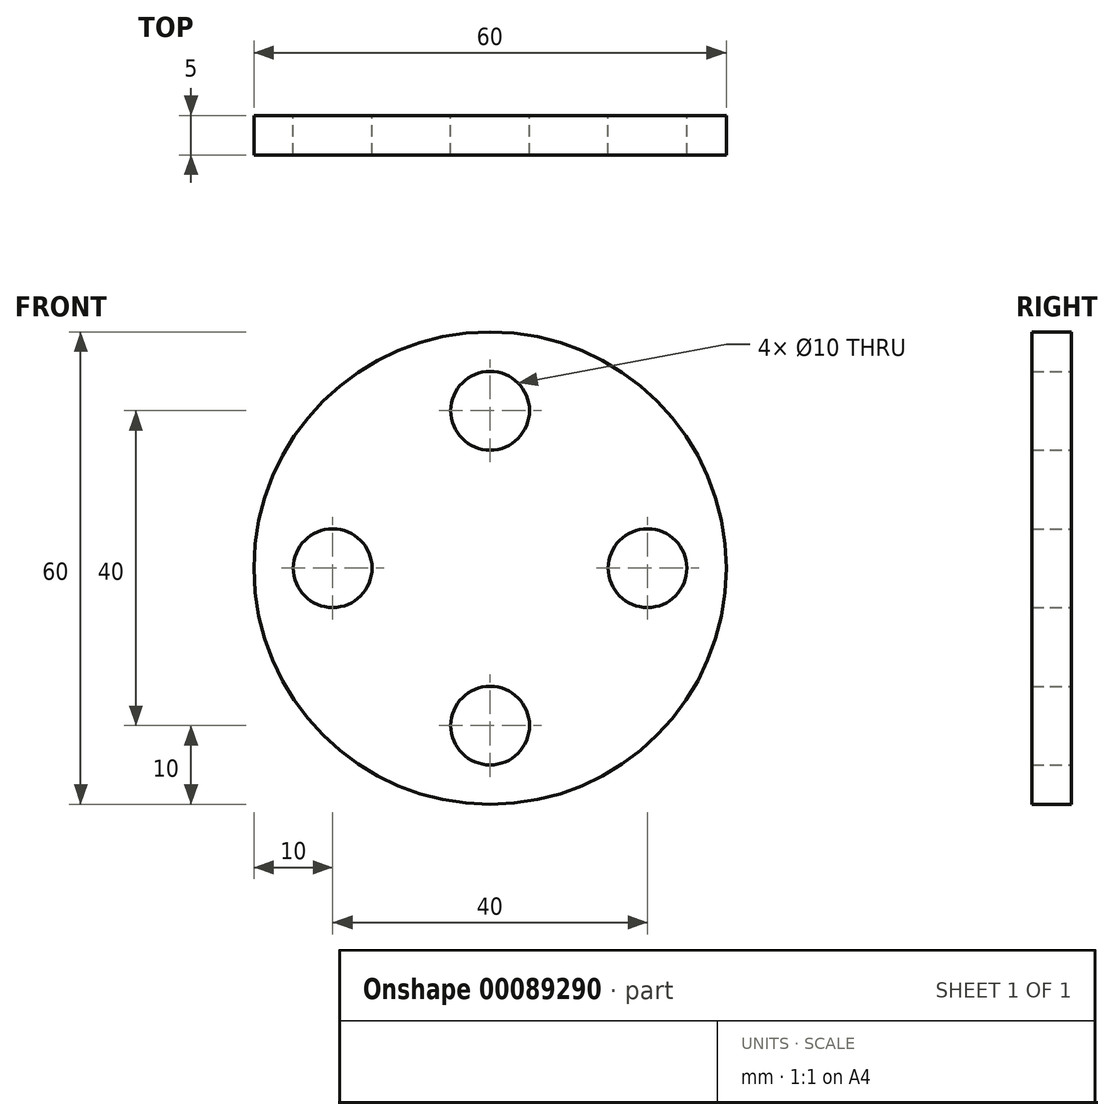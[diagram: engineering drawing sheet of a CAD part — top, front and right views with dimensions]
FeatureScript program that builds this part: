
annotation { "Feature Type Name" : "Feature", "Feature Type Description" : "" }
export const myFeature = defineFeature(function(context is Context, id is Id, definition is map)
    precondition{}
    {
        {
            var Q0;
            Q0=qCreatedBy(makeId("Front.planeOp"),FACE);
            var sketch = newSketch(context, id + "F0", { "sketchPlane" : qUnion([Q0])});
            skLineSegment(sketch, "E0", {"start": v(0, 37.15) * mm, "end": v(0, -35.7) * mm, "construction": true});
            skLineSegment(sketch, "E1", {"start": v(-62.01, 0) * mm, "end": v(63.82, 0) * mm, "construction": true});
            skCircle(sketch, "E2", {"center": v(0, 0) * mm, "radius": 30 * mm});
            skCircle(sketch, "E3", {"center": v(0, 0) * mm, "radius": 20 * mm, "construction": true});
            skCircle(sketch, "E4", {"center": v(-20, 0) * mm, "radius": 5 * mm});
            skCircle(sketch, "E5.MirrorC", {"center": v(20, 0) * mm, "radius": 5 * mm});
            skCircle(sketch, "E6", {"center": v(0, 20) * mm, "radius": 5 * mm});
            skCircle(sketch, "E7.MirrorC", {"center": v(0, -20) * mm, "radius": 5 * mm});
            skSolve(sketch);
        }
        {
            var Q0;
            Q0=makeQuery(id+"F0.imprint","IMPRINT",FACE,{"disambiguationData":[TD([[makeQuery(id+"F0.imprint","IMPRINT",EDGE,{"derivedFrom":sQuery(id+"F0.wireOp",EDGE,"E2")}),1.0]])]});
            extrude(context, id + "F1", {"entities" : qUnion([Q0]), "depth" : 5 * mm});
        }
    });
